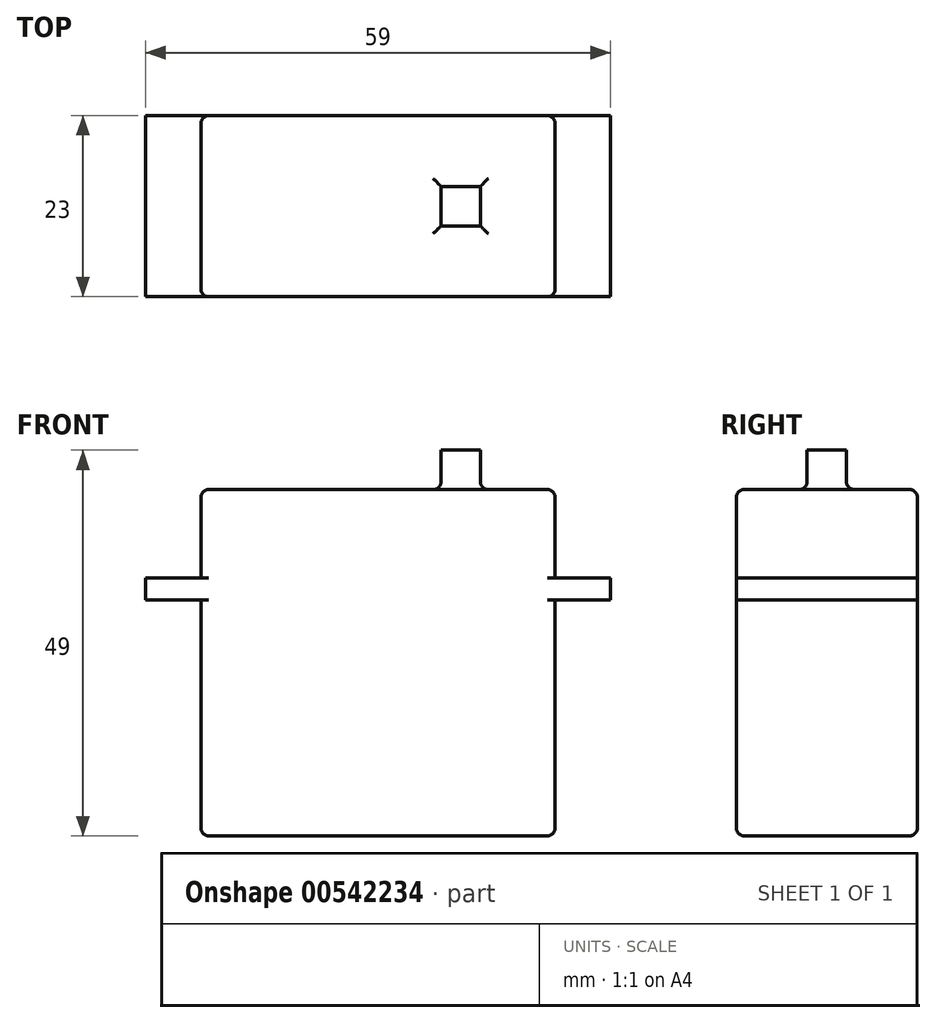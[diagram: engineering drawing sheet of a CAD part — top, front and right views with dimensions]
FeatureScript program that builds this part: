
annotation { "Feature Type Name" : "Feature", "Feature Type Description" : "" }
export const myFeature = defineFeature(function(context is Context, id is Id, definition is map)
    precondition{}
    {
        {
            var Q0;
            Q0=qCreatedBy(makeId("Front.planeOp"),FACE);
            var sketch = newSketch(context, id + "F0", { "sketchPlane" : qUnion([Q0])});
            skLineSegment(sketch, "E0.bottom", {"start": v(0, 0) * mm, "end": v(45, 0) * mm});
            skLineSegment(sketch, "E0.top", {"start": v(0, 44) * mm, "end": v(45, 44) * mm});
            skLineSegment(sketch, "E0.left", {"start": v(0, 0) * mm, "end": v(0, 44) * mm});
            skLineSegment(sketch, "E0.right", {"start": v(45, 0) * mm, "end": v(45, 44) * mm});
            skSolve(sketch);
        }
        {
            var Q0;
            Q0 = qSketchRegion(id + "F0", true);
            extrude(context, id + "F1", {"entities" : qUnion([Q0]), "depth" : 23 * mm, "offsetDistance" : 25 * mm});
        }
        {
            var Q0;
            Q0=makeQuery(id+"F1.opExtrude","SWEPT_FACE",FACE,{"disambiguationData":[OSD([sQuery(id+"F0.wireOp",EDGE,"E0.top")])]});
            var sketch = newSketch(context, id + "F2", { "sketchPlane" : qUnion([Q0])});
            skLineSegment(sketch, "E1.bottom", {"start": v(30.5, -14) * mm, "end": v(35.5, -14) * mm});
            skLineSegment(sketch, "E1.top", {"start": v(30.5, -9) * mm, "end": v(35.5, -9) * mm});
            skLineSegment(sketch, "E1.left", {"start": v(30.5, -14) * mm, "end": v(30.5, -9) * mm});
            skLineSegment(sketch, "E1.right", {"start": v(35.5, -14) * mm, "end": v(35.5, -9) * mm});
            skLineSegment(sketch, "E2", {"start": v(33, -9) * mm, "end": v(33, -14) * mm, "construction": true});
            skLineSegment(sketch, "E3", {"start": v(45, -11.5) * mm, "end": v(0, -11.5) * mm, "construction": true});
            skPoint(sketch, "E4", {"position": v(33, -11.5) * mm});
            skSolve(sketch);
        }
        {
            var Q0;
            Q0 = qSketchRegion(id + "F2", true);
            extrude(context, id + "F3", {"entities" : qUnion([Q0]), "operationType" : NewBodyOperationType.ADD, "depth" : 5 * mm, "offsetDistance" : 25 * mm});
        }
        {
            var Q0;
            Q0=makeQuery(id+"F1.opExtrude","SWEPT_FACE",FACE,{"disambiguationData":[OSD([sQuery(id+"F0.wireOp",EDGE,"E0.top")])]});
            cPlane(context, id + "F4", {"entities" : qUnion([Q0]), "cplaneType" : CPlaneType.OFFSET, "offset" : 14 * mm, "oppositeDirection" : true, "width" : 150 * mm, "height" : 150 * mm});
        }
        {
            var Q0;
            Q0=qCreatedBy(id+"F4.planeOp",FACE);
            var sketch = newSketch(context, id + "F5", { "sketchPlane" : qUnion([Q0])});
            skLineSegment(sketch, "E5.bottom", {"start": v(-7, -23) * mm, "end": v(52, -23) * mm});
            skLineSegment(sketch, "E5.top", {"start": v(-7, 0) * mm, "end": v(52, 0) * mm});
            skLineSegment(sketch, "E5.left", {"start": v(-7, -23) * mm, "end": v(-7, 0) * mm});
            skLineSegment(sketch, "E5.right", {"start": v(52, -23) * mm, "end": v(52, 0) * mm});
            skSolve(sketch);
        }
        {
            var Q0;
            Q0 = qSketchRegion(id + "F5", true);
            extrude(context, id + "F6", {"entities" : qUnion([Q0]), "operationType" : NewBodyOperationType.ADD, "depth" : 2.75 * mm, "offsetDistance" : 25 * mm});
        }
        {
            var Q0;
            Q0=makeQuery(id+"F1.opExtrude","SWEPT_FACE",FACE,{"disambiguationData":[OSD([sQuery(id+"F0.wireOp",EDGE,"E0.top")])]});
            var Q1;
            Q1=makeQuery(id+"F1.opExtrude","SWEPT_FACE",FACE,{"disambiguationData":[OSD([sQuery(id+"F0.wireOp",EDGE,"E0.bottom")])]});
            var Q2;
            {var subQ1=sQuery(id+"F0.wireOp",EDGE,"E0.right");var subQ2=sQuery(id+"F0.wireOp",EDGE,"E0.bottom");Q2=makeQuery(id+"F6.boolean.opBoolean","SPLIT",EDGE,{"disambiguationData":[TD([makeQuery(id+"F1.opExtrude","SWEPT_FACE",FACE,{"disambiguationData":[OSD([subQ2])]})])],"derivedFrom":makeQuery(id+"F1.opExtrude","CAP_EDGE",EDGE,{"disambiguationData":[OSD([subQ1])],"isStart":false})});}
            var Q3;
            {var subQ1=sQuery(id+"F0.wireOp",EDGE,"E0.bottom");var subQ2=sQuery(id+"F0.wireOp",EDGE,"E0.right");Q3=makeQuery(id+"F6.boolean.opBoolean","SPLIT",EDGE,{"disambiguationData":[TD([makeQuery(id+"F1.opExtrude","SWEPT_FACE",FACE,{"disambiguationData":[OSD([subQ1])]})])],"derivedFrom":makeQuery(id+"F1.opExtrude","CAP_EDGE",EDGE,{"disambiguationData":[OSD([subQ2])],"isStart":true})});}
            var Q4;
            {var subQ1=sQuery(id+"F0.wireOp",EDGE,"E0.left");var subQ2=sQuery(id+"F0.wireOp",EDGE,"E0.bottom");Q4=makeQuery(id+"F6.boolean.opBoolean","SPLIT",EDGE,{"disambiguationData":[TD([makeQuery(id+"F1.opExtrude","SWEPT_FACE",FACE,{"disambiguationData":[OSD([subQ2])]})])],"derivedFrom":makeQuery(id+"F1.opExtrude","CAP_EDGE",EDGE,{"disambiguationData":[OSD([subQ1])],"isStart":false})});}
            var Q5;
            {var subQ0=sQuery(id+"F0.wireOp",EDGE,"E0.left");var subQ2=sQuery(id+"F0.wireOp",EDGE,"E0.top");Q5=makeQuery(id+"F6.boolean.opBoolean","SPLIT",EDGE,{"disambiguationData":[TD([makeQuery(id+"F1.opExtrude","SWEPT_FACE",FACE,{"disambiguationData":[OSD([subQ2])]})])],"derivedFrom":makeQuery(id+"F1.opExtrude","CAP_EDGE",EDGE,{"disambiguationData":[OSD([subQ0])],"isStart":false})});}
            var Q6;
            {var subQ0=sQuery(id+"F0.wireOp",EDGE,"E0.right");var subQ2=sQuery(id+"F0.wireOp",EDGE,"E0.top");Q6=makeQuery(id+"F6.boolean.opBoolean","SPLIT",EDGE,{"disambiguationData":[TD([makeQuery(id+"F1.opExtrude","SWEPT_FACE",FACE,{"disambiguationData":[OSD([subQ2])]})])],"derivedFrom":makeQuery(id+"F1.opExtrude","CAP_EDGE",EDGE,{"disambiguationData":[OSD([subQ0])],"isStart":false})});}
            var Q7;
            {var subQ1=sQuery(id+"F0.wireOp",EDGE,"E0.right");var subQ2=sQuery(id+"F0.wireOp",EDGE,"E0.top");Q7=makeQuery(id+"F6.boolean.opBoolean","SPLIT",EDGE,{"disambiguationData":[TD([makeQuery(id+"F1.opExtrude","SWEPT_FACE",FACE,{"disambiguationData":[OSD([subQ2])]})])],"derivedFrom":makeQuery(id+"F1.opExtrude","CAP_EDGE",EDGE,{"disambiguationData":[OSD([subQ1])],"isStart":true})});}
            var Q8;
            {var subQ1=sQuery(id+"F0.wireOp",EDGE,"E0.left");var subQ2=sQuery(id+"F0.wireOp",EDGE,"E0.top");Q8=makeQuery(id+"F6.boolean.opBoolean","SPLIT",EDGE,{"disambiguationData":[TD([makeQuery(id+"F1.opExtrude","SWEPT_FACE",FACE,{"disambiguationData":[OSD([subQ2])]})])],"derivedFrom":makeQuery(id+"F1.opExtrude","CAP_EDGE",EDGE,{"disambiguationData":[OSD([subQ1])],"isStart":true})});}
            var Q9;
            {var subQ1=sQuery(id+"F0.wireOp",EDGE,"E0.bottom");var subQ2=sQuery(id+"F0.wireOp",EDGE,"E0.left");Q9=makeQuery(id+"F6.boolean.opBoolean","SPLIT",EDGE,{"disambiguationData":[TD([makeQuery(id+"F1.opExtrude","SWEPT_FACE",FACE,{"disambiguationData":[OSD([subQ1])]})])],"derivedFrom":makeQuery(id+"F1.opExtrude","CAP_EDGE",EDGE,{"disambiguationData":[OSD([subQ2])],"isStart":true})});}
            fillet(context, id + "F7", {"entities" : qUnion([Q0, Q1, Q2, Q3, Q4, Q5, Q6, Q7, Q8, Q9]), "radius" : 1 * mm, "tangentPropagation" : true, "allowEdgeOverflow" : false});
        }
    });
